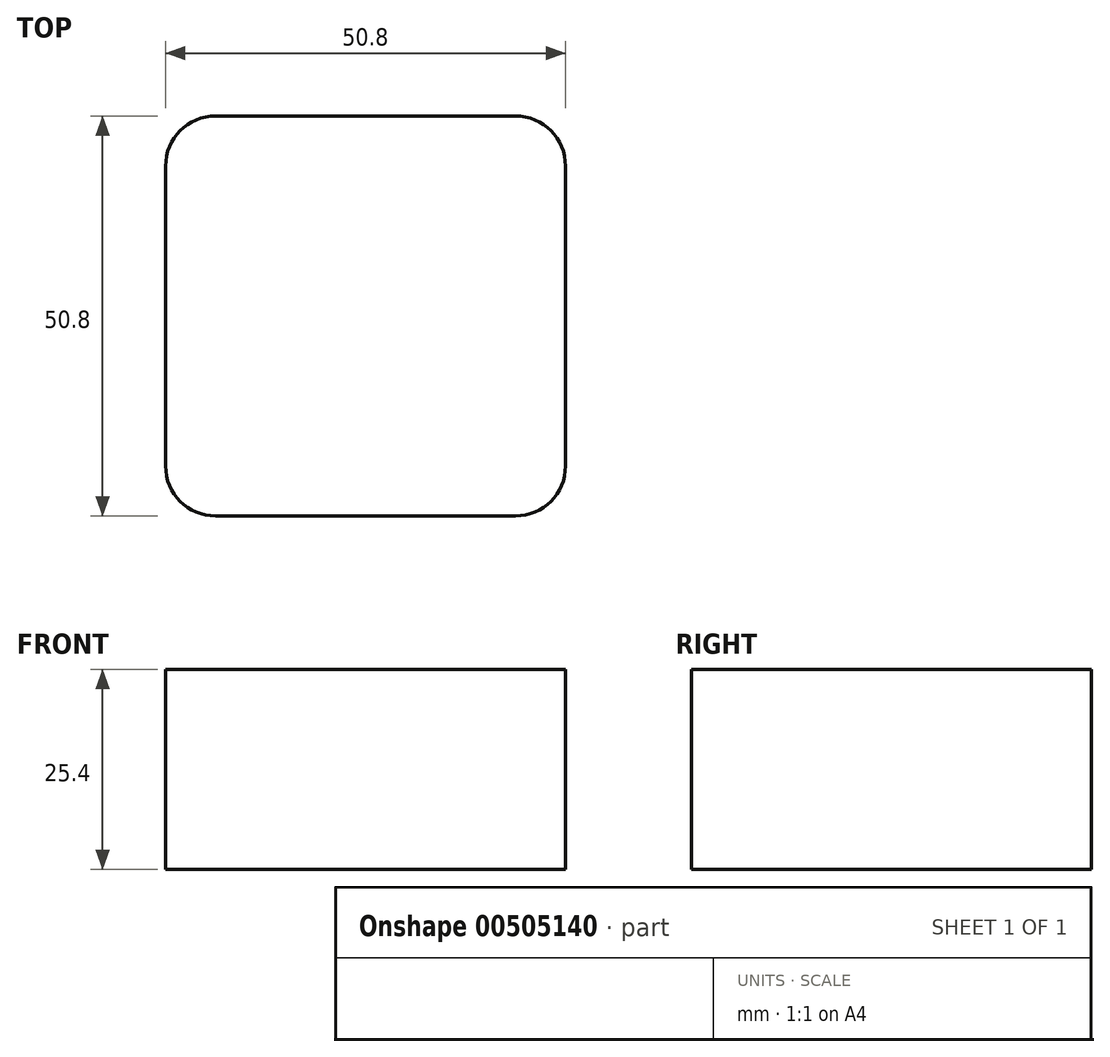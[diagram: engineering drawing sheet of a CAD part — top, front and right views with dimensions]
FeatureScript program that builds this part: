
annotation { "Feature Type Name" : "Feature", "Feature Type Description" : "" }
export const myFeature = defineFeature(function(context is Context, id is Id, definition is map)
    precondition{}
    {
        {
            var Q0;
            Q0=qCreatedBy(makeId("Top.planeOp"),FACE);
            var sketch = newSketch(context, id + "F0", { "sketchPlane" : qUnion([Q0])});
            skLineSegment(sketch, "E0", {"start": v(0, 25.4) * mm, "end": v(-25.4, 25.4) * mm});
            skLineSegment(sketch, "E1.MirrorCS", {"start": v(0, 25.4) * mm, "end": v(25.4, 25.4) * mm});
            skLineSegment(sketch, "E2.MirrorCS", {"start": v(0, -25.4) * mm, "end": v(-25.4, -25.4) * mm});
            skLineSegment(sketch, "E3.MirrorCS", {"start": v(0, -25.4) * mm, "end": v(25.4, -25.4) * mm});
            skLineSegment(sketch, "E4", {"start": v(-25.4, 25.4) * mm, "end": v(-25.4, -25.4) * mm});
            skLineSegment(sketch, "E5", {"start": v(25.4, 25.4) * mm, "end": v(25.4, -25.4) * mm});
            skSolve(sketch);
        }
        {
            var Q0;
            Q0 = qSketchRegion(id + "F0", true);
            extrude(context, id + "F1", {"entities" : qUnion([Q0]), "endBound" : BoundingType.SYMMETRIC, "depth" : 25.4 * mm});
        }
        {
            var Q0;
            Q0=makeQuery(id+"F1.opExtrude","SWEPT_EDGE",EDGE,{"disambiguationData":[OSD([sQuery(id+"F0.wireOp",EDGE,"E0"),sQuery(id+"F0.wireOp",EDGE,"E4")])]});
            var Q1;
            Q1=makeQuery(id+"F1.opExtrude","SWEPT_EDGE",EDGE,{"disambiguationData":[OSD([sQuery(id+"F0.wireOp",EDGE,"E1.MirrorCS"),sQuery(id+"F0.wireOp",EDGE,"E5")])]});
            var Q2;
            Q2=makeQuery(id+"F1.opExtrude","SWEPT_EDGE",EDGE,{"disambiguationData":[OSD([sQuery(id+"F0.wireOp",EDGE,"E3.MirrorCS"),sQuery(id+"F0.wireOp",EDGE,"E5")])]});
            var Q3;
            Q3=makeQuery(id+"F1.opExtrude","SWEPT_EDGE",EDGE,{"disambiguationData":[OSD([sQuery(id+"F0.wireOp",EDGE,"E2.MirrorCS"),sQuery(id+"F0.wireOp",EDGE,"E4")])]});
            fillet(context, id + "F2", {"entities" : qUnion([Q0, Q1, Q2, Q3]), "radius" : 6.35 * mm, "tangentPropagation" : true, "allowEdgeOverflow" : false});
        }
    });
